# Revit family: STS-705P_RV17_LOD_400
name_source: partatom
category: Электрооборудование
revit_build: Autodesk Revit 2017 (Build: 20170118_1100(x64)
units: mm (PartAtom-declared; Revit-internal decimal feet)

## family parameters
Всегда вертикально = Да
Конфигурация панели = Два столбца, слева направо
На основе рабочей плоскости = Нет
Общий = Нет
При загрузке вырезать с полостями = Нет
Размер круглого соединителя = Использовать диаметр
Тип детали = Щит
Точка расчета площади = Нет

## types (1)
- STS-705P
    ADSK_URL страницы изделия = https://stilsoft.ru
    ADSK_Единица измерения = шт.
    ADSK_Завод-изготовитель = ООО «Основа Безопасности»
    ADSK_Классификация нагрузок = Считыватель
    ADSK_Количество = 1
    ADSK_Марка = СТВФ.431295.136
    ADSK_Масса = 0.1
    ADSK_Наименование = STS-705P
    ADSK_Размер_Высота = 105 мм
    ADSK_Размер_Длина = 43 мм
    ADSK_Размер_Ширина = 21 мм
    ADSK_Ток = 0 А
    Антенна = Встроенная
    Время считывания, мс = 200
    Диапазон рабочих температур, °С = от минус 40 до плюс 50
    Идентификаторы = Em - Marin
    Интерфейс = RS-485
    Напряжение = 12
    Напряжение питания постоянного тока, В = 7,5-13,8
    Номинальная дальность считывания идентификационного признака, до, см = 4-7 (зависит от идентификатора доступа)
    Рабочая частота, кГц = 125
    Расстояние между считывателями, см = 10-20
    Удаленность от контроллера Wiegand 42, не более, м = 100
